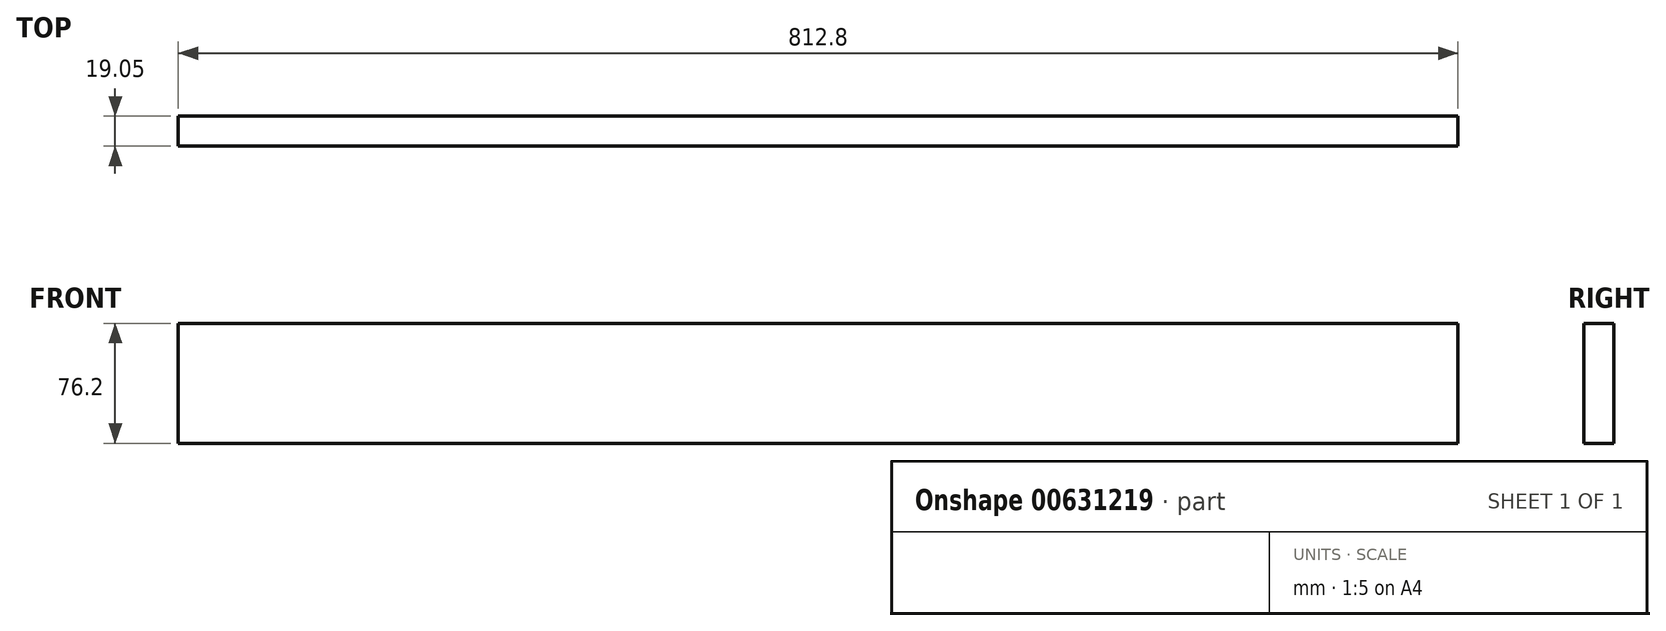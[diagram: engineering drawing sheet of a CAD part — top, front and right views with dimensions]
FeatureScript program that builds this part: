
annotation { "Feature Type Name" : "Feature", "Feature Type Description" : "" }
export const myFeature = defineFeature(function(context is Context, id is Id, definition is map)
    precondition{}
    {
        {
            var Q0;
            Q0=qCreatedBy(makeId("Front.planeOp"),FACE);
            var sketch = newSketch(context, id + "F0", { "sketchPlane" : qUnion([Q0])});
            skLineSegment(sketch, "E0.bottom", {"start": v(0, 0) * mm, "end": v(812.8, 0) * mm});
            skLineSegment(sketch, "E0.top", {"start": v(0, 76.2) * mm, "end": v(812.8, 76.2) * mm});
            skLineSegment(sketch, "E0.left", {"start": v(0, 0) * mm, "end": v(0, 76.2) * mm});
            skLineSegment(sketch, "E0.right", {"start": v(812.8, 0) * mm, "end": v(812.8, 76.2) * mm});
            skSolve(sketch);
        }
        {
            var Q0;
            Q0=qSketchRegion(id+"Fzz42SO8jX8z24B_0",true);
            var Q1;
            Q1=makeQuery(id+"F0.imprint","IMPRINT",FACE,{"disambiguationData":[TD([[makeQuery(id+"F0.imprint","IMPRINT",EDGE,{"derivedFrom":sQuery(id+"F0.wireOp",EDGE,"E0.bottom")}),1.0]])]});
            extrude(context, id + "F1", {"entities" : qUnion([Q0, Q1]), "depth" : -19.05 * mm, "offsetDistance" : 25.4 * mm});
        }
    });
